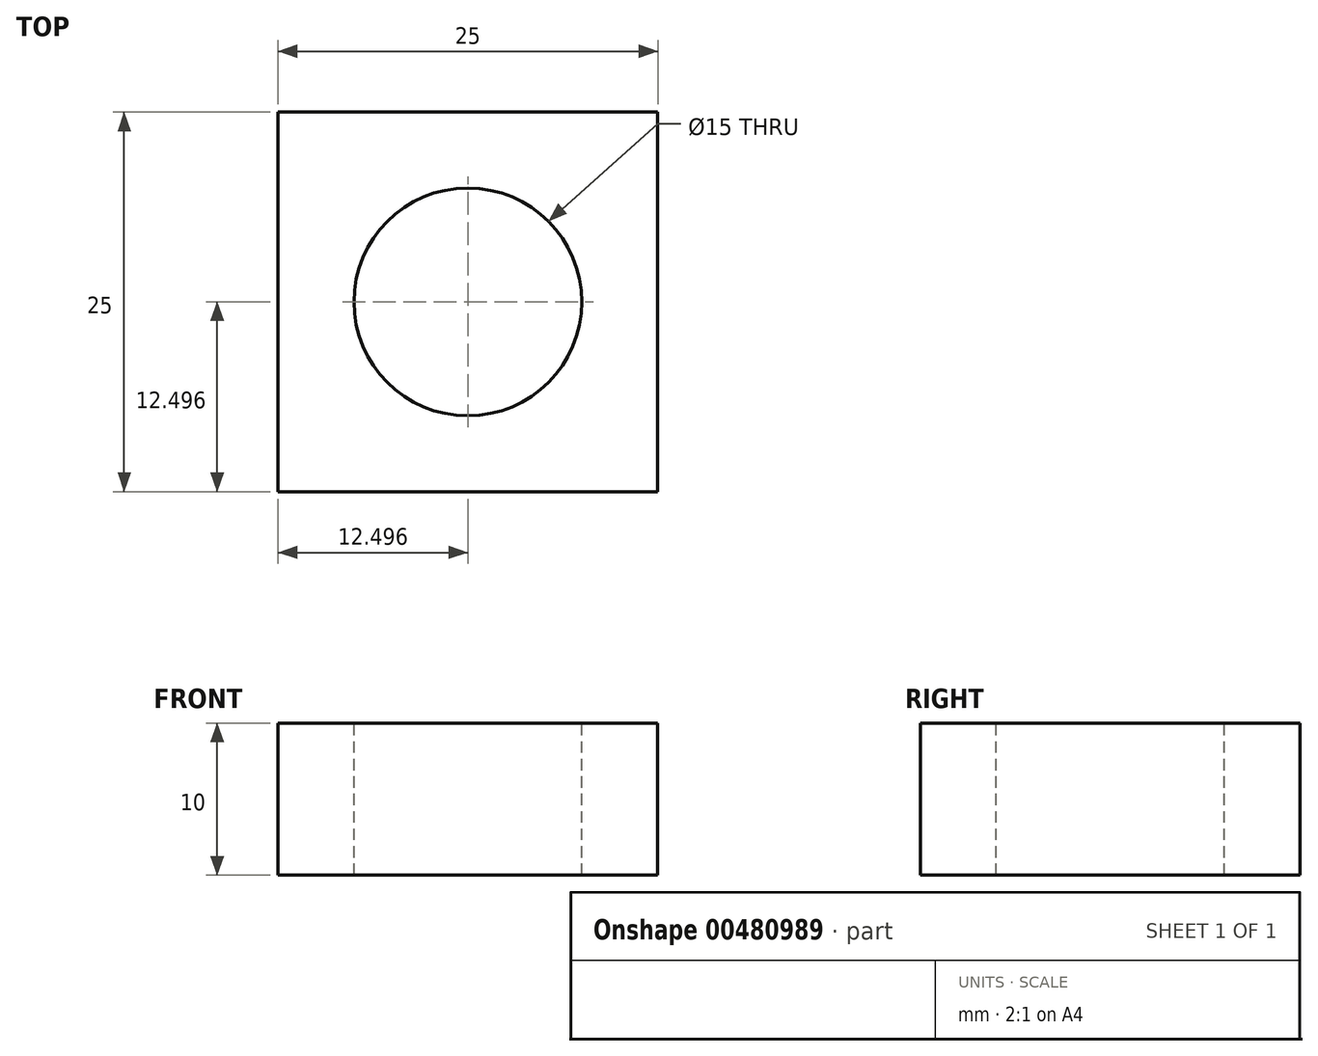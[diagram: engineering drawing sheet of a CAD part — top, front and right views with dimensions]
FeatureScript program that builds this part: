
annotation { "Feature Type Name" : "Feature", "Feature Type Description" : "" }
export const myFeature = defineFeature(function(context is Context, id is Id, definition is map)
    precondition{}
    {
        {
            var Q0;
            Q0=qCreatedBy(makeId("Top.planeOp"),FACE);
            var sketch = newSketch(context, id + "F0", { "sketchPlane" : qUnion([Q0])});
            skLineSegment(sketch, "E0.bottom", {"start": v(-13.67, 15.5) * mm, "end": v(11.33, 15.5) * mm});
            skLineSegment(sketch, "E0.top", {"start": v(-13.67, -9.5) * mm, "end": v(11.33, -9.5) * mm});
            skLineSegment(sketch, "E0.left", {"start": v(-13.67, 15.5) * mm, "end": v(-13.67, -9.5) * mm});
            skLineSegment(sketch, "E0.right", {"start": v(11.33, 15.5) * mm, "end": v(11.33, -9.5) * mm});
            skSolve(sketch);
        }
        {
            var Q0;
            Q0=makeQuery(id+"F0.imprint","IMPRINT",FACE,{"disambiguationData":[TD([[makeQuery(id+"F0.imprint","IMPRINT",EDGE,{"derivedFrom":sQuery(id+"F0.wireOp",EDGE,"E0.bottom")}),-1.0]])]});
            extrude(context, id + "F1", {"entities" : qUnion([Q0]), "depth" : 10 * mm});
        }
        {
            var Q0;
            Q0=makeQuery(id+"F1.opExtrude","CAP_FACE",FACE,{"disambiguationData":[OSD([sQuery(id+"F0.wireOp",EDGE,"E0.bottom"),sQuery(id+"F0.wireOp",EDGE,"E0.top"),sQuery(id+"F0.wireOp",EDGE,"E0.left"),sQuery(id+"F0.wireOp",EDGE,"E0.right")])],"isStart":false});
            var sketch = newSketch(context, id + "F2", { "sketchPlane" : qUnion([Q0])});
            skCircle(sketch, "E1", {"center": v(-1.17, 3) * mm, "radius": 7.5 * mm});
            skPoint(sketch, "E1.centerSnap0", {"position": v(-13.67, 3) * mm});
            skPoint(sketch, "E1.centerSnap1", {"position": v(-1.17, -9.5) * mm});
            skSolve(sketch);
        }
        {
            var Q0;
            Q0=makeQuery(id+"F2.imprint","IMPRINT",FACE,{"disambiguationData":[TD([[makeQuery(id+"F2.imprint","IMPRINT",EDGE,{"derivedFrom":sQuery(id+"F2.wireOp",EDGE,"E1")}),1.0]])]});
            extrude(context, id + "F3", {"entities" : qUnion([Q0]), "operationType" : NewBodyOperationType.REMOVE, "endBound" : BoundingType.THROUGH_ALL, "oppositeDirection" : true, "depth" : 25 * mm});
        }
    });
